# Revit family: Faucet_Touchless-Lavatory-KOHLER-Components-K-104M36_1
name_source: partatom
category: Plumbing Fixtures
units: mm (PartAtom-declared; Revit-internal decimal feet)

## family parameters
Cut with Voids When Loaded = No
Host = Face
OmniClass Number = 23.31.11.00
OmniClass Title = Faucets
Part Type = Normal
Room Calculation Point = No
Round Connector Dimension = Use Diameter
Shared = No

## types (2) — shared parameters
ADA Compliant = No
Assembly Code = D2010
CW Connection = No
Cold Water Inlet = Cold Water Inlet
Date Modified = 07/14/2023
Default Elevation = 36"
Description = Deck Mount Single Supply
Drain Included = Yes
Finish = Kohler-Metal-CP-Polished_Chrome
HW Connection = Yes
Height = 8 1/8"
Hot Water Inlet = Hot Water Inlet
Length = 6 5/8"
Manufacturer = Kohler Co.
Master Format 2014 = 22 41 39
Master Format 2014 Name = Residential Faucets, Supplies, and Trim
Material = Premium Metal Construction
Pressure = 0.00 psi
Product Documentation Link = https://www.us.kohler.com _spec_US-CA_Kohler_en.pdf
Product Name = Components
Product Page URL = http://www.us.kohler.com
Spout Reach = 6 5/8"
Tempered Water Inlet = Tempered Water Inlet
URL = https://www.us.kohler.com
Vent Connection = No
Waste Connection = No
Waste Water Outlet = Waste Water Outlet
WaterSense Certified = No
Width = 2 3/8"

## per-type parameters (varying)
| type | Flow Rate | Model | Type |
| 0.5 GPM, CP-Polished Chrome | 1 GPM | K-104M36-SANA-CP | 1 |
| 0.35 GPM, CP-Polished Chrome | 0 GPM | K-104M36-SATA-CP | 2 |

## geometry (parser evidence)
native form markers: Sweep x6
no freeform markers — native parametric forms only
